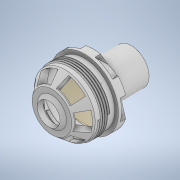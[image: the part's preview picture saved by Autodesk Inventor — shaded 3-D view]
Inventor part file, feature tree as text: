
AUTODESK INVENTOR PART (.ipt)
format: ipt  version: 2020 (Build 240168000, 168)  size: 611,840 bytes
history: native  units: mm
features: sketch x18, extrude x11, chamfer x7, revolve x5, projected_geometry x5, plane x4, helix x2, pattern_circular x2, split x1
ambient origin geometry x8: Origin, YZ Plane, XZ Plane, XY Plane, X Axis, Y Axis, Z Axis, Center Point
bodies: Solid1 (feature_tree)
feature tree (55):
  extrude  "Extrusion1"  Depth=2.0mm
  chamfer  "Chamfer1"  Distance=2.0mm
  revolve  "Revolution1"  [1 undecoded]
  extrude  "Extrusion2"  Depth=18.75mm
  sketch  "Sketch6"  dims[d17=1.6mm]
  helix  "Coil2"  [1 undecoded]
  chamfer  "Chamfer4"  Distance=10.0mm
  chamfer  "Chamfer5"  Distance=0.65mm Angle=45.0deg
  extrude  "Extrusion4"  Depth=42.0mm
  extrude  "Extrusion6"  Depth=3.3mm
  extrude  "Extrusion7"  Depth=1.2mm
  helix  "Coil3"  [1 undecoded]
  extrude  "Extrusion8"  Depth=3.0mm TaperAngle=0.0deg
  revolve  "Revolution2"  [1 undecoded]
  plane  "Work Plane2"
  split  "Split1"
  revolve  "Revolution3"  [1 undecoded]
  plane  "Work Plane3"
  plane  "Work Plane4"
  extrude  "Extrusion10"  Depth=10.0mm
  extrude  "Extrusion11"  Depth=10.0mm TaperAngle=0.0deg
  revolve  "Revolution4"  Angle=135.0deg
  extrude  "Extrusion12"  TaperAngle=90.0deg  [1 undecoded]
  revolve  "Revolution5"  [1 undecoded]
  plane  "Work Plane5"
  extrude  "Extrusion13"  Depth=10.0mm
  chamfer  "Chamfer7"  Distance=20.0mm
  pattern_circular  "Circular Pattern2"  [2 undecoded]
  extrude  "Extrusion15"  Depth=10.0mm
  pattern_circular  "Circular Pattern4"  Angle=90.0deg  [1 undecoded]
  chamfer  "Chamfer8"  [1 undecoded]
  chamfer  "Chamfer9"  [1 undecoded]
  chamfer  "Chamfer10"  Distance=42.0mm
  sketch  "Sketch1"  dims[d0=18.0mm d1=2.0mm d2=2.0mm d3=0.0mm]
  sketch  "Sketch4"  dims[d4=2.0mm d5=2.0mm d6=45.0deg d10=12.25mm]
  sketch  "Sketch5"  dims[d11=8.0mm d12=18.75mm d14=1.5mm]
  projected_geometry  "Projected Loop1"
  sketch  "Sketch8"  dims[d18=90.0deg d19=10.0mm d20=0.0mm]
  sketch  "Sketch9"  dims[d21=1.0mm]
  sketch  "Sketch10"  dims[d22=1.0mm]
  sketch  "Sketch11"  dims[d23=1.5mm]
  sketch  "Sketch12"  dims[d24=0.8mm]
  sketch  "Sketch13"  dims[d42=0.1mm]
  sketch  "Sketch14"  dims[d43=1.5mm]
  sketch  "Sketch16"  dims[d44=6.0mm d45=10.0mm d46=0.0mm d47=90.0deg d48=90.0deg d49=0.0mm d50=0.0mm d51=0.65mm d52=4.0mm d53=45.0deg]
  sketch  "Sketch17"  dims[d54=0.65mm d55=4.0mm d56=45.0deg d57=42.0mm]
  projected_geometry  "Projected Loop3"
  sketch  "Sketch18"  dims[d58=28.0mm d59=0.0mm d60=3.3mm]
  sketch  "Sketch19"  dims[d61=1.2mm d62=1.2mm d65=12.0mm d66=0.0mm]
  sketch  "Sketch20"  dims[d67=25.0mm d68=3.0mm d69=0.0mm]
  projected_geometry  "Projected Loop4"
  projected_geometry  "Projected Loop5"
  sketch  "Sketch21"  dims[d73=1.5mm d74=1.0mm]
  projected_geometry  "Projected Loop6"
  sketch  "Sketch23"  dims[d75=0.8mm d76=1.5mm d77=28.0mm d78=10.0mm d79=0.0mm d80=90.0deg d81=90.0deg d82=0.0mm d83=0.0mm d84=45.0mm d85=20.0mm d86=0.0mm d87=135.0deg d88=90.0deg d89=0.0mm d91=11.25mm d92=20.0mm d93=11.0mm d94=1.6mm d95=90.0deg d96=-20.0mm d108=-17.3mm d109=42.0mm d110=4.8mm d111=0.0mm d112=31.068147mm d113=21.0mm d115=2.8mm d116=0.0mm d117=0.473mm d118=90.0deg d119=2.8mm d120=0.0mm d121=135.0deg d122=90.0deg d123=-32.0mm d124=4.363323mm d125=10.0mm d126=0.0mm d127=6.5mm d128=9.75mm d129=45.0deg d130=60.0mm d131=360.0deg d136=37.5mm d137=24.5mm d138=31.0mm d139=5.0mm d140=10.0mm d141=0.0mm d145=5.0mm d146=6.0mm d147=5.0mm d148=6.0mm d149=60.0mm d150=360.0deg d152=6.0mm d153=2.0mm d154=45.0deg d155=6.0mm d156=2.0mm d157=45.0deg d158=2.0mm d159=2.0mm d160=45.0deg d70=0.5mm d71=0.872665mm d72=0.5mm d90=0.872665mm]
note: 12 required parameter values undecoded (feature->parameter linkage not recoverable at this tier; creation-order binding heuristic only, values carry confidence <= 0.55)